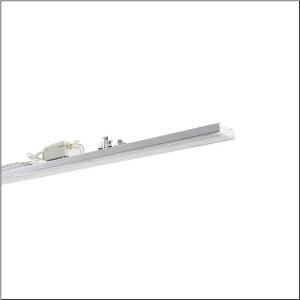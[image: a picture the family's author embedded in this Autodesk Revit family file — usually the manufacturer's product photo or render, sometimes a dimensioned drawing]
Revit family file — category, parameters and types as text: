
# Revit family: licross_r__21_recessed_mo_52te14dn49xg_1976
name_source: partatom
category: Lighting Fixtures
units: mm (PartAtom-declared; Revit-internal decimal feet)

## family parameters
Cut with Voids When Loaded = No
Host = Face
Light Source = No
Part Type = Normal
Room Calculation Point = No
Round Connector Dimension = Use Diameter
Shared = No

## types (1)
- --- (1 x LED, 9470 lm, 58 W, 4000K)
    Apparent Load = 58 VA
    CIE Flux Codes = 56 84 97 100 100
    Color Rendering = 80
    Color Temperature = 4000K
    Default Elevation = 1800 mm
    Description = Licross® 21 Recessed MO, luminaire insert, of sheet steel, galvanised, coil coated, white, length: 1.500mm, width: 66mm, height: 67mm, LED rated luminous flux: 9.470lm, light colour: 840, control gear: DALI 2, with plug, 5-pole, with phase selection, mains connection: 220..240V, AC, 50/60Hz, rated input power: 58W, halogen-free wiring, primary light control with lens, of plastic, primary optical cover: cover, of PMMA, light emission: direct distribution, primary light characteristic: asymmetric, protection rating (complete): IP54, insulation class (complete): insulation class I (protective earthing), certification: CE, ENEC, VDE, UKCA, protection symbol: D if used in an environment with non-conductive dust loads with corresponding accessories, impact resistance: IK06, permissible ambient temperature for indoor applications: -25..+35°C, corresponds to IFS (International Featured Standards) requirements for safety and quality in the food industry, reducing of maximum allowable ambient temperature of 5°C with ceiling mounting, LABS conformity tested according to VDMA 24364:2018-05, packaging unit: 1 piece
    Height = 58 mm
    Lamp = 1 x LED
    Lamp Light Flux = 9470 lm
    Lamp Power = 58 W
    Lamp count = 1
    Length = 1500 mm
    Luminous efficacy = 163 lm/W
    Manufacturer = Siteco
    ModVariant = No
    Model = 52TE14DN49XG
    Mounting Place = Ceiling
    Mounting Type = Pendant
    Number of Poles = 1
    OnlyDefault = Yes
    Power Factor = 1
    Product Name = Licross® 21 Recessed MO
    Product group = luminaire insert
    ProductGroupID = 901
    Protection Class = Protection class I
    Protection Degree = IP 54
    RLX_Detail_Level = 1
    RLX_Emergency_Light_Flux = 0 lm
    RLX_Emergency_Type = 0
    RLX_Emergency_Type_DB = No
    RlxData = <blob elided: 25021 chars, md5=1d93ff34>
    Socket = socket
    Standby Power = 0 W
    System Light Flux = 9470 lm
    System Power = 58 W
    Type Comments = factory setting: luminous flux: 100 % | dim-lin: 254 | 390 mA
    Type Image = l_1296930.jpg
    URL = http://relux.com
    VarID = @adj_059327
    Voltage = 0 V
    Weight = 0.00 kg
    Width = 66 mm

## geometry (parser evidence)
native form markers: Blend x4, Sweep x9
no freeform markers — native parametric forms only
